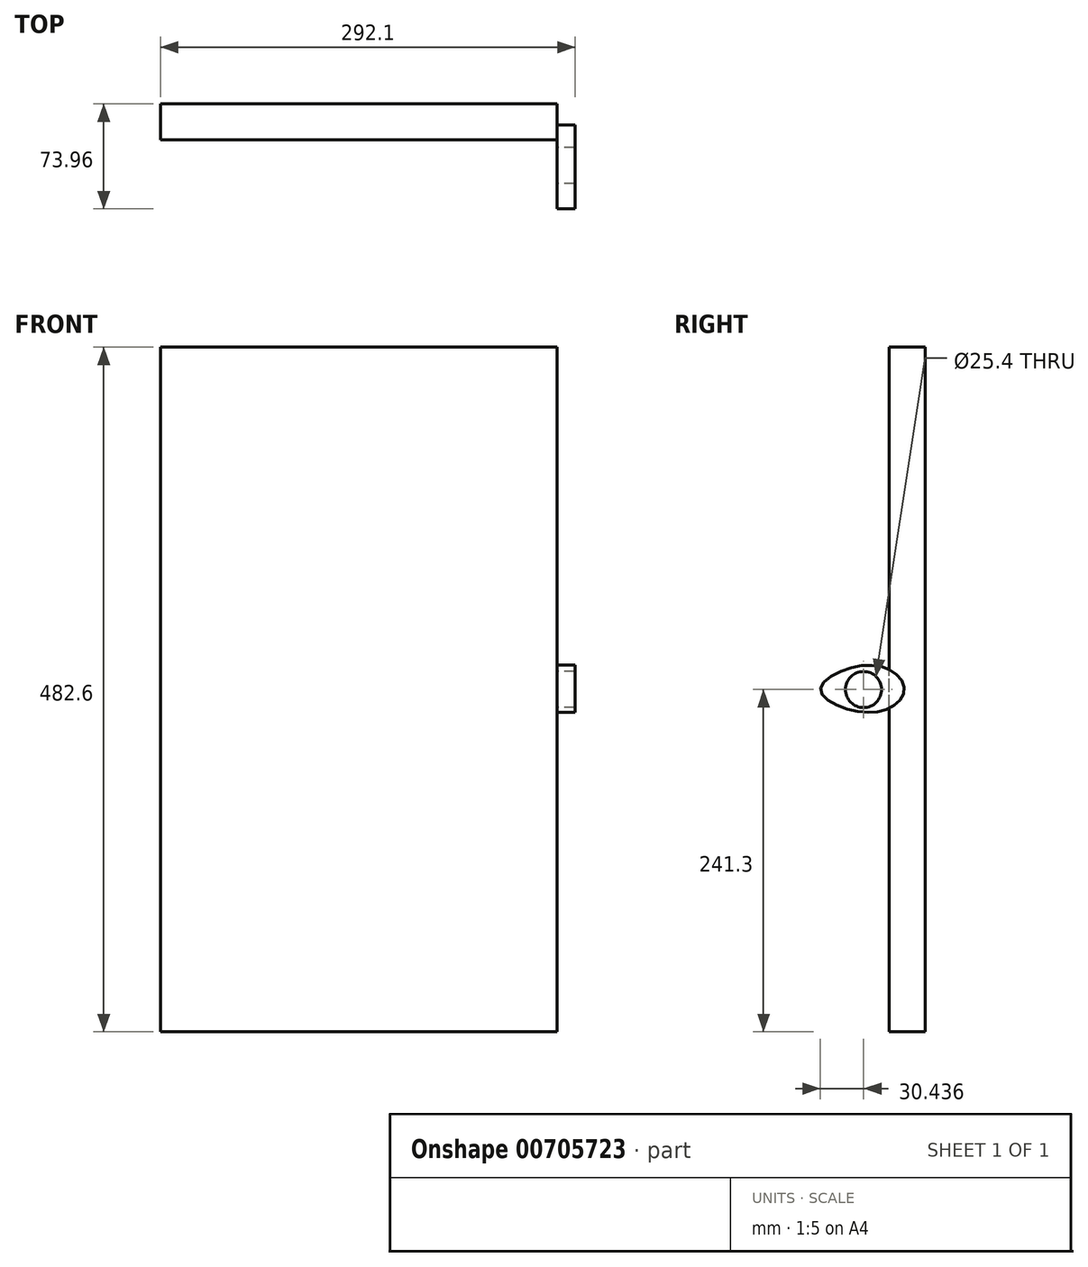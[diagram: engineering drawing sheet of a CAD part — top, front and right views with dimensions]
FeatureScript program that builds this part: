
annotation { "Feature Type Name" : "Feature", "Feature Type Description" : "" }
export const myFeature = defineFeature(function(context is Context, id is Id, definition is map)
    precondition{}
    {
        {
            var Q0;
            Q0=qCreatedBy(makeId("Front.planeOp"),FACE);
            var sketch = newSketch(context, id + "F0", { "sketchPlane" : qUnion([Q0])});
            skLineSegment(sketch, "E0.bottom", {"start": v(139.7, -241.3) * mm, "end": v(-139.7, -241.3) * mm});
            skLineSegment(sketch, "E0.top", {"start": v(139.7, 241.3) * mm, "end": v(-139.7, 241.3) * mm});
            skLineSegment(sketch, "E0.left", {"start": v(139.7, -241.3) * mm, "end": v(139.7, 241.3) * mm});
            skLineSegment(sketch, "E0.right", {"start": v(-139.7, -241.3) * mm, "end": v(-139.7, 241.3) * mm});
            skPoint(sketch, "E0.middle", {"position": v(0, 0) * mm});
            skSolve(sketch);
        }
        {
            var Q0;
            Q0 = qSketchRegion(id + "F0", true);
            extrude(context, id + "F1", {"entities" : qUnion([Q0]), "depth" : 25.4 * mm, "offsetDistance" : 25.4 * mm});
        }
        {
            var Q0;
            Q0=makeQuery(id+"F1.opExtrude","SWEPT_FACE",FACE,{"disambiguationData":[OSD([sQuery(id+"F0.wireOp",EDGE,"E0.left")])]});
            var sketch = newSketch(context, id + "F2", { "sketchPlane" : qUnion([Q0])});
            skFitSpline(sketch, "E1", {"points": [v(-25.4, 14.03) * mm, v(-53.86, 14.8) * mm, v(-73.96, 0) * mm, v(-53.86, -14.04) * mm, v(-25.4, -13.28) * mm, v(-14.8, 0) * mm, v(-25.4, 14.03) * mm]});
            skCircle(sketch, "E2", {"center": v(-43.52, 0) * mm, "radius": 12.7 * mm});
            skSolve(sketch);
        }
        {
            var Q0;
            {var subQ0=sQuery(id+"F2.wireOp",EDGE,"E1");var subQ1=makeQuery(id+"F1.opExtrude","CAP_EDGE",EDGE,{"disambiguationData":[OSD([sQuery(id+"F0.wireOp",EDGE,"E0.left")])],"isStart":false});var subQ2=makeQuery(id+"F2.imprint","INTERSECT",VERTEX,{"disambiguationData":[OD(0.0)],"derivedFrom":[subQ1,subQ0]});Q0=makeQuery(id+"F2.imprint","IMPRINT",FACE,{"disambiguationData":[TD([[makeQuery(id+"F2.imprint","IMPRINT",EDGE,{"disambiguationData":[TD([[subQ2,1.0]])],"derivedFrom":subQ0}),1.0]])]});}
            var Q1;
            {var subQ0=sQuery(id+"F2.wireOp",EDGE,"E1");var subQ1=makeQuery(id+"F1.opExtrude","CAP_EDGE",EDGE,{"disambiguationData":[OSD([sQuery(id+"F0.wireOp",EDGE,"E0.left")])],"isStart":false});var subQ2=makeQuery(id+"F2.imprint","INTERSECT",VERTEX,{"disambiguationData":[OD(0.0)],"derivedFrom":[subQ1,subQ0]});Q1=makeQuery(id+"F2.imprint","IMPRINT",FACE,{"disambiguationData":[TD([[makeQuery(id+"F2.imprint","IMPRINT",EDGE,{"disambiguationData":[TD([[subQ2,-1.0]])],"derivedFrom":subQ0}),1.0]])]});}
            extrude(context, id + "F3", {"entities" : qUnion([Q0, Q1]), "operationType" : NewBodyOperationType.ADD, "depth" : 12.7 * mm, "offsetDistance" : 25.4 * mm});
        }
    });
